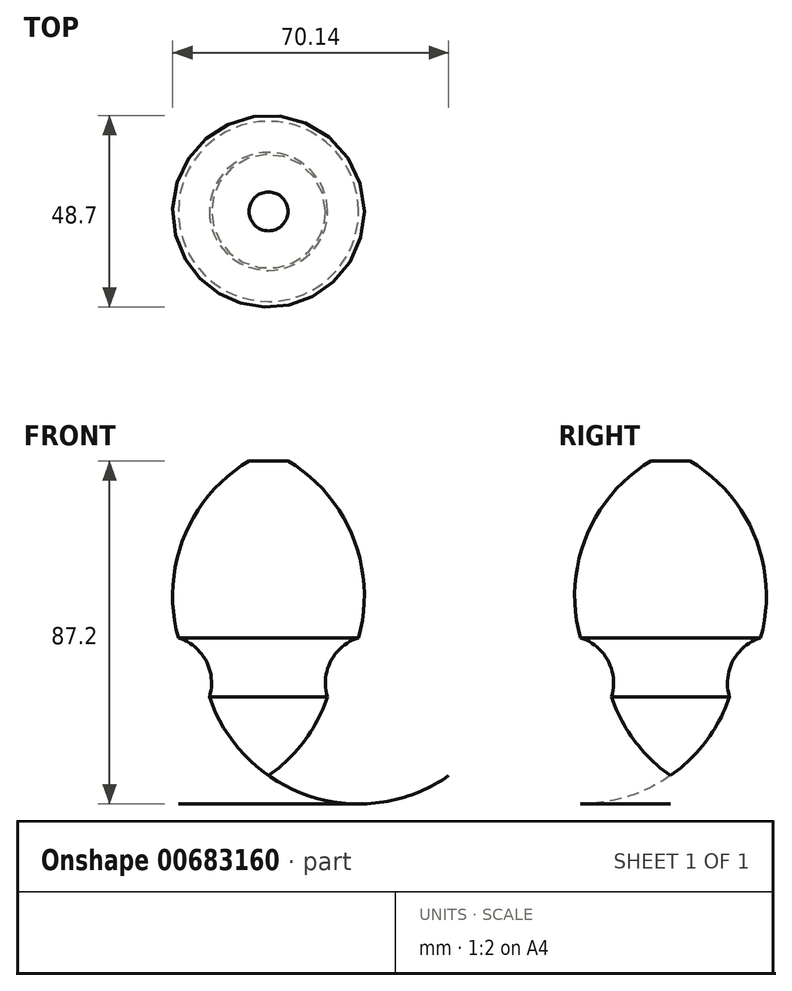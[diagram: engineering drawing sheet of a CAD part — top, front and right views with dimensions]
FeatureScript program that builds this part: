
annotation { "Feature Type Name" : "Feature", "Feature Type Description" : "" }
export const myFeature = defineFeature(function(context is Context, id is Id, definition is map)
    precondition{}
    {
        {
            var Q0;
            Q0=qCreatedBy(makeId("Front.planeOp"),FACE);
            var sketch = newSketch(context, id + "F0", { "sketchPlane" : qUnion([Q0])});
            skLineSegment(sketch, "E0", {"start": v(0, 0) * mm, "end": v(0, -80) * mm});
            skLineSegment(sketch, "E1", {"start": v(0, 0) * mm, "end": v(0, 0) * mm});
            skLineSegment(sketch, "E2", {"start": v(0, 0) * mm, "end": v(4.94, 0) * mm});
            skLineSegment(sketch, "E3", {"start": v(0, -60) * mm, "end": v(15, -60) * mm});
            skLineSegment(sketch, "E4", {"start": v(0, -45) * mm, "end": v(22.9, -45) * mm});
            skArc(sketch, "E5", {"start": v(22.9, -45) * mm, "mid": v(21.5, -19.47) * mm, "end": v(4.94, 0) * mm});
            skPoint(sketch, "E6", {"position": v(22.9, -45) * mm});
            skArc(sketch, "E7", {"start": v(22.9, -45) * mm, "mid": v(15.85, -50.87) * mm, "end": v(15, -60) * mm});
            skArc(sketch, "E8", {"start": v(0, -80) * mm, "mid": v(9.1, -71.2) * mm, "end": v(15, -60) * mm});
            skSolve(sketch);
        }
        {
            var Q0;
            {var subQ0=sQuery(id+"F0.wireOp",EDGE,"E2");Q0=makeQuery(id+"F0.imprint","IMPRINT",FACE,{"disambiguationData":[TD([[makeQuery(id+"F0.imprint","IMPRINT",EDGE,{"derivedFrom":subQ0}),-1.0]])]});}
            var Q1;
            {var subQ0=sQuery(id+"F0.wireOp",EDGE,"E3");Q1=makeQuery(id+"F0.imprint","IMPRINT",FACE,{"disambiguationData":[TD([[makeQuery(id+"F0.imprint","IMPRINT",EDGE,{"derivedFrom":subQ0}),1.0]])]});}
            var Q2;
            {var subQ2=sQuery(id+"F0.wireOp",EDGE,"E3");Q2=makeQuery(id+"F0.imprint","IMPRINT",FACE,{"disambiguationData":[TD([[makeQuery(id+"F0.imprint","IMPRINT",EDGE,{"derivedFrom":subQ2}),-1.0]])]});}
            var Q3;
            Q3=sQuery(id+"F0.wireOp",EDGE,"E0");
            revolve(context, id + "F1", {"entities" : qUnion([Q0, Q1, Q2]), "axis" : qUnion([Q3]), "revolveType" : RevolveType.FULL});
        }
    });
